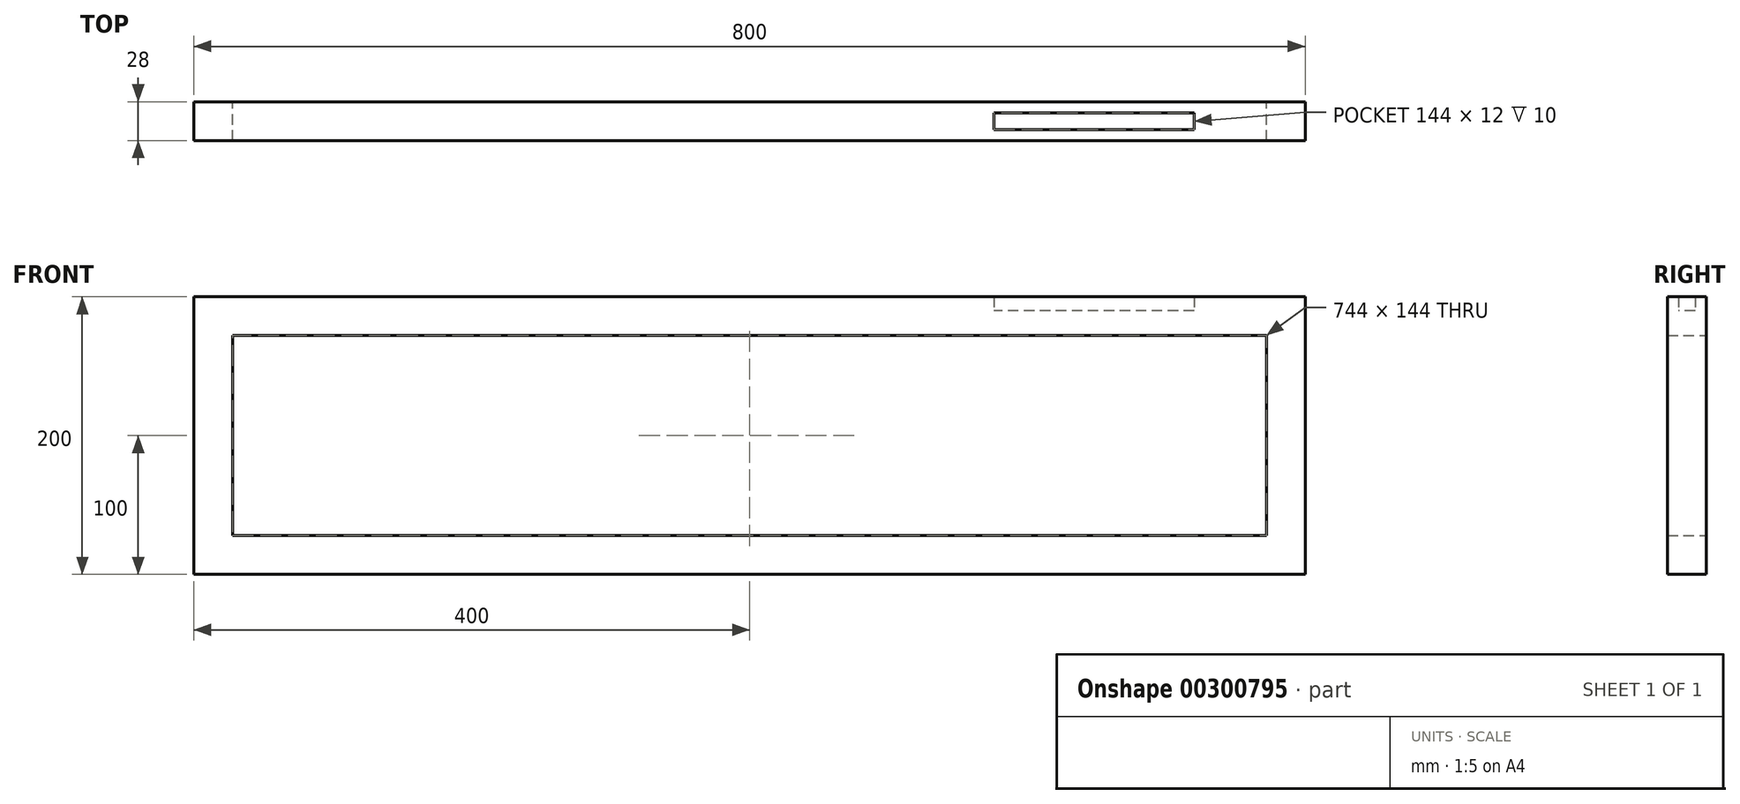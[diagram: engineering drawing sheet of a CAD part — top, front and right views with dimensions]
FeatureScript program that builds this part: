
annotation { "Feature Type Name" : "Feature", "Feature Type Description" : "" }
export const myFeature = defineFeature(function(context is Context, id is Id, definition is map)
    precondition{}
    {
        {
            var Q0;
            Q0=qCreatedBy(makeId("Front.planeOp"),FACE);
            var sketch = newSketch(context, id + "F0", { "sketchPlane" : qUnion([Q0])});
            skLineSegment(sketch, "E0.bottom", {"start": v(0, 0) * mm, "end": v(2000, 0) * mm});
            skLineSegment(sketch, "E0.top", {"start": v(0, -500) * mm, "end": v(2000, -500) * mm});
            skLineSegment(sketch, "E0.left", {"start": v(0, 0) * mm, "end": v(0, -500) * mm});
            skLineSegment(sketch, "E0.right", {"start": v(2000, 0) * mm, "end": v(2000, -500) * mm});
            skLineSegment(sketch, "E1", {"start": v(70, 0) * mm, "end": v(70, -500) * mm});
            skLineSegment(sketch, "E2", {"start": v(0, -70) * mm, "end": v(2000, -70) * mm});
            skLineSegment(sketch, "E3", {"start": v(1930, 0) * mm, "end": v(1930, -500) * mm});
            skLineSegment(sketch, "E4", {"start": v(0, -430) * mm, "end": v(2000, -430) * mm});
            skSolve(sketch);
        }
        {
            var Q0;
            Q0=qSketchRegion(id+"F0",true);
            extrude(context, id + "F1", {"entities" : qUnion([Q0]), "depth" : 70 * mm});
        }
        {
            var Q0;
            Q0=makeQuery(id+"F1.opExtrude","SWEPT_FACE",FACE,{"disambiguationData":[OSD([sQuery(id+"F0.wireOp",EDGE,"E0.bottom")])]});
            var sketch = newSketch(context, id + "F2", { "sketchPlane" : qUnion([Q0])});
            skLineSegment(sketch, "E5.bottom", {"start": v(1800, -20) * mm, "end": v(1440, -20) * mm});
            skLineSegment(sketch, "E5.top", {"start": v(1800, -50) * mm, "end": v(1440, -50) * mm});
            skLineSegment(sketch, "E5.left", {"start": v(1800, -20) * mm, "end": v(1800, -50) * mm});
            skLineSegment(sketch, "E5.right", {"start": v(1440, -20) * mm, "end": v(1440, -50) * mm});
            skSolve(sketch);
        }
        {
            var Q0;
            Q0=makeQuery(id+"F2.imprint","IMPRINT",FACE,{"disambiguationData":[TD([[makeQuery(id+"F2.imprint","IMPRINT",EDGE,{"derivedFrom":sQuery(id+"F2.wireOp",EDGE,"E5.bottom")}),1.0]])]});
            extrude(context, id + "F3", {"entities" : qUnion([Q0]), "operationType" : NewBodyOperationType.REMOVE, "depth" : 25 * mm, "hasSecondDirection" : true, "secondDirectionOppositeDirection" : true, "secondDirectionDepth" : 25 * mm});
        }
        {
            var Q0;
            Q0=makeQuery(id+"F1.opExtrude","SWEPT_BODY",BODY,{"disambiguationData":[OSD([sQuery(id+"F0.wireOp",EDGE,"E0.bottom"),sQuery(id+"F0.wireOp",EDGE,"E0.top"),sQuery(id+"F0.wireOp",EDGE,"E0.left"),sQuery(id+"F0.wireOp",EDGE,"E0.right"),sQuery(id+"F0.wireOp",EDGE,"E1"),sQuery(id+"F0.wireOp",EDGE,"E2"),sQuery(id+"F0.wireOp",EDGE,"E3"),sQuery(id+"F0.wireOp",EDGE,"E4")])]});
            var Q1;
            Q1=makeQuery(id+"F1.opExtrude","CAP_VERTEX",VERTEX,{"disambiguationData":[OSD([sQuery(id+"F0.wireOp",EDGE,"E0.top"),sQuery(id+"F0.wireOp",EDGE,"E0.right")])],"isStart":false});
            var Q2;
            Q2=makeQuery(id+"F1.opExtrude","CAP_VERTEX",VERTEX,{"disambiguationData":[OSD([sQuery(id+"F0.wireOp",EDGE,"E0.top"),sQuery(id+"F0.wireOp",EDGE,"E0.right")])],"isStart":false});
            transform(context, id + "F4", {"entities" : qUnion([Q0]), "transformType" : TransformType.SCALE_UNIFORMLY, "scale" : 0.4, "scalePoint" : qUnion([Q2]), "makeCopy" : false});
        }
    });
